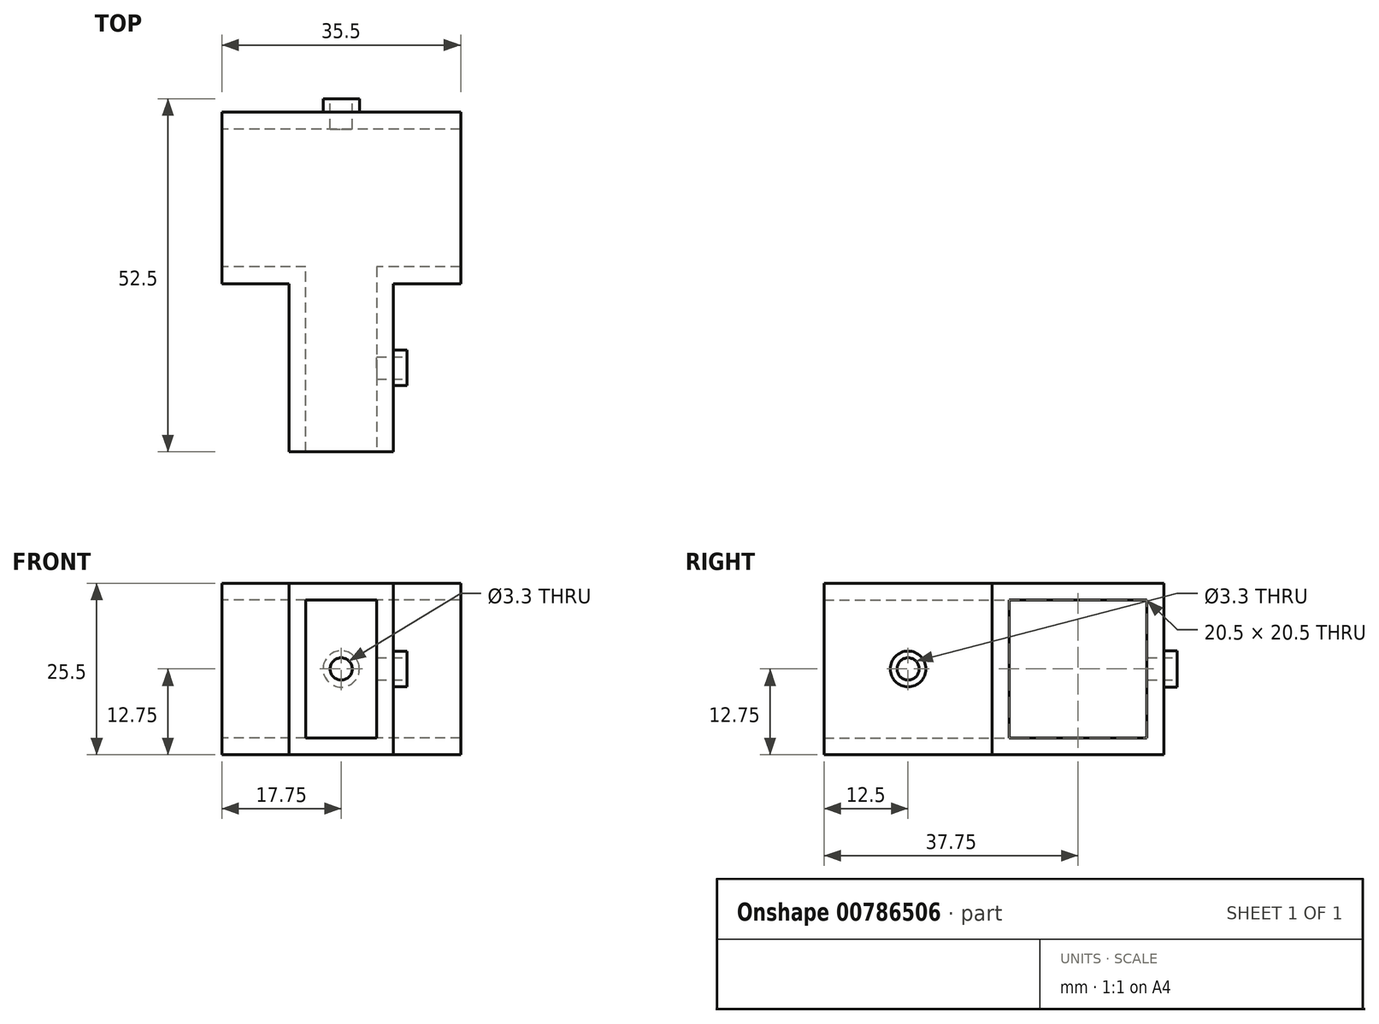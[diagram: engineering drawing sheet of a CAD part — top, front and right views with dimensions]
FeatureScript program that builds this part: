
annotation { "Feature Type Name" : "Feature", "Feature Type Description" : "" }
export const myFeature = defineFeature(function(context is Context, id is Id, definition is map)
    precondition{}
    {
        {
            var Q0;
            Q0=qCreatedBy(makeId("Front.planeOp"),FACE);
            var sketch = newSketch(context, id + "F0", { "sketchPlane" : qUnion([Q0])});
            skLineSegment(sketch, "E0.bottom", {"start": v(-17.75, 12.75) * mm, "end": v(17.75, 12.75) * mm});
            skLineSegment(sketch, "E0.top", {"start": v(-17.75, -12.75) * mm, "end": v(17.75, -12.75) * mm});
            skLineSegment(sketch, "E0.left", {"start": v(-17.75, 15.55) * mm, "end": v(-17.75, -12.75) * mm});
            skLineSegment(sketch, "E0.right", {"start": v(17.75, 12.75) * mm, "end": v(17.75, -12.75) * mm});
            skPoint(sketch, "E1", {"position": v(0, 0) * mm});
            skPoint(sketch, "E1.positionSnap0", {"position": v(17.75, 0) * mm});
            skPoint(sketch, "E1.positionSnap1", {"position": v(0, 12.75) * mm});
            skSolve(sketch);
        }
        {
            var Q0;
            Q0=qSketchRegion(id+"F0",true);
            extrude(context, id + "F1", {"entities" : qUnion([Q0]), "depth" : 25.5 * mm, "offsetDistance" : 25 * mm});
        }
        {
            var Q0;
            Q0=makeQuery(id+"F1.opExtrude","SWEPT_FACE",FACE,{"disambiguationData":[OSD([sQuery(id+"F0.wireOp",EDGE,"E0.left")])]});
            var sketch = newSketch(context, id + "F2", { "sketchPlane" : qUnion([Q0])});
            skLineSegment(sketch, "E2.bottom", {"start": v(2.5, 10.25) * mm, "end": v(23, 10.25) * mm});
            skLineSegment(sketch, "E2.top", {"start": v(2.5, -10.25) * mm, "end": v(23, -10.25) * mm});
            skLineSegment(sketch, "E2.left", {"start": v(2.5, 10.25) * mm, "end": v(2.5, -10.25) * mm});
            skLineSegment(sketch, "E2.right", {"start": v(23, 10.25) * mm, "end": v(23, -10.25) * mm});
            skSolve(sketch);
        }
        {
            var Q0;
            Q0=qSketchRegion(id+"F2",true);
            extrude(context, id + "F3", {"entities" : qUnion([Q0]), "operationType" : NewBodyOperationType.REMOVE, "oppositeDirection" : true, "depth" : 35.5 * mm, "offsetDistance" : 25 * mm});
        }
        {
            var Q0;
            Q0=makeQuery(id+"F1.opExtrude","CAP_FACE",FACE,{"disambiguationData":[OSD([sQuery(id+"F0.wireOp",EDGE,"E0.bottom"),sQuery(id+"F0.wireOp",EDGE,"E0.top"),sQuery(id+"F0.wireOp",EDGE,"E0.left"),sQuery(id+"F0.wireOp",EDGE,"E0.right")])],"isStart":false});
            var sketch = newSketch(context, id + "F4", { "sketchPlane" : qUnion([Q0])});
            skLineSegment(sketch, "E3.bottom", {"start": v(-7.75, 12.75) * mm, "end": v(7.75, 12.75) * mm});
            skLineSegment(sketch, "E3.top", {"start": v(-7.75, -12.75) * mm, "end": v(7.75, -12.75) * mm});
            skLineSegment(sketch, "E3.left", {"start": v(-7.75, 12.75) * mm, "end": v(-7.75, -12.75) * mm});
            skLineSegment(sketch, "E3.right", {"start": v(7.75, 12.75) * mm, "end": v(7.75, -12.75) * mm});
            skSolve(sketch);
        }
        {
            var Q0;
            Q0=qSketchRegion(id+"F4",true);
            extrude(context, id + "F5", {"entities" : qUnion([Q0]), "operationType" : NewBodyOperationType.ADD, "depth" : 25 * mm, "offsetDistance" : 25 * mm});
        }
        {
            var Q0;
            Q0=makeQuery(id+"F5.opExtrude","CAP_FACE",FACE,{"disambiguationData":[OSD([sQuery(id+"F4.wireOp",EDGE,"E3.bottom"),sQuery(id+"F4.wireOp",EDGE,"E3.top"),sQuery(id+"F4.wireOp",EDGE,"E3.left"),sQuery(id+"F4.wireOp",EDGE,"E3.right")])],"isStart":false});
            var sketch = newSketch(context, id + "F6", { "sketchPlane" : qUnion([Q0])});
            skLineSegment(sketch, "E4.bottom", {"start": v(-15.25, 10.25) * mm, "end": v(5.25, 10.25) * mm});
            skLineSegment(sketch, "E4.top", {"start": v(-15.25, -10.25) * mm, "end": v(5.25, -10.25) * mm});
            skLineSegment(sketch, "E4.left", {"start": v(-15.25, 10.25) * mm, "end": v(-15.25, -10.25) * mm});
            skLineSegment(sketch, "E4.right", {"start": v(5.25, 10.25) * mm, "end": v(5.25, -10.25) * mm});
            skSolve(sketch);
        }
        {
            var Q0;
            Q0=qSketchRegion(id+"F6",true);
            extrude(context, id + "F7", {"entities" : qUnion([Q0]), "operationType" : NewBodyOperationType.REMOVE, "oppositeDirection" : true, "depth" : 38 * mm, "offsetDistance" : 25 * mm});
        }
        {
            var Q0;
            Q0=makeQuery(id+"F5.opExtrude","SWEPT_FACE",FACE,{"disambiguationData":[OSD([sQuery(id+"F4.wireOp",EDGE,"E3.right")])]});
            var sketch = newSketch(context, id + "F8", { "sketchPlane" : qUnion([Q0])});
            skCircle(sketch, "E5", {"center": v(-38, 0) * mm, "radius": 2.65 * mm});
            skPoint(sketch, "E5.centerSnap0", {"position": v(-38, -12.75) * mm});
            skPoint(sketch, "E5.centerSnap1", {"position": v(-50.5, 0) * mm});
            skSolve(sketch);
        }
        {
            var Q0;
            Q0=qSketchRegion(id+"F8",true);
            extrude(context, id + "F9", {"entities" : qUnion([Q0]), "operationType" : NewBodyOperationType.ADD, "depth" : 2 * mm, "offsetDistance" : 25 * mm});
        }
        {
            var Q0;
            Q0=makeQuery(id+"F9.opExtrude","CAP_FACE",FACE,{"disambiguationData":[OSD([sQuery(id+"F8.wireOp",EDGE,"E5")])],"isStart":false});
            var sketch = newSketch(context, id + "F10", { "sketchPlane" : qUnion([Q0])});
            skCircle(sketch, "E6", {"center": v(-38, 0) * mm, "radius": 1.65 * mm});
            skSolve(sketch);
        }
        {
            var Q0;
            Q0=qSketchRegion(id+"F10",true);
            extrude(context, id + "F11", {"entities" : qUnion([Q0]), "operationType" : NewBodyOperationType.REMOVE, "endBound" : BoundingType.THROUGH_ALL, "oppositeDirection" : true, "depth" : 30 * mm, "offsetDistance" : 25 * mm});
        }
        {
            var Q0;
            Q0=makeQuery(id+"F1.opExtrude","CAP_FACE",FACE,{"disambiguationData":[OSD([sQuery(id+"F0.wireOp",EDGE,"E0.bottom"),sQuery(id+"F0.wireOp",EDGE,"E0.top"),sQuery(id+"F0.wireOp",EDGE,"E0.left"),sQuery(id+"F0.wireOp",EDGE,"E0.right")])],"isStart":true});
            var sketch = newSketch(context, id + "F12", { "sketchPlane" : qUnion([Q0])});
            skCircle(sketch, "E7", {"center": v(0, 0) * mm, "radius": 2.7 * mm});
            skSolve(sketch);
        }
        {
            var Q0;
            Q0=qSketchRegion(id+"F12",true);
            extrude(context, id + "F13", {"entities" : qUnion([Q0]), "operationType" : NewBodyOperationType.ADD, "depth" : 2 * mm, "offsetDistance" : 25 * mm});
        }
        {
            var Q0;
            Q0=makeQuery(id+"F13.opExtrude","CAP_FACE",FACE,{"disambiguationData":[OSD([sQuery(id+"F12.wireOp",EDGE,"E7")])],"isStart":false});
            var sketch = newSketch(context, id + "F14", { "sketchPlane" : qUnion([Q0])});
            skCircle(sketch, "E8", {"center": v(0, 0) * mm, "radius": 1.65 * mm});
            skSolve(sketch);
        }
        {
            var Q0;
            Q0=qSketchRegion(id+"F14",true);
            extrude(context, id + "F15", {"entities" : qUnion([Q0]), "operationType" : NewBodyOperationType.REMOVE, "oppositeDirection" : true, "depth" : 5.5 * mm, "offsetDistance" : 25 * mm});
        }
        {
            var Q0;
            Q0=makeQuery(id+"F7.boolean.opBoolean","MERGE",FACE,{"derivedFrom":[makeQuery(id+"F3.boolean.opBoolean","COPY",FACE,{"derivedFrom":makeQuery(id+"F3.opExtrude","SWEPT_FACE",FACE,{"disambiguationData":[OSD([sQuery(id+"F2.wireOp",EDGE,"E2.top")])]})}),makeQuery(id+"F7.opExtrude","SWEPT_FACE",FACE,{"disambiguationData":[OSD([sQuery(id+"F6.wireOp",EDGE,"E4.top")])]})]});
            var sketch = newSketch(context, id + "F16", { "sketchPlane" : qUnion([Q0])});
            skLineSegment(sketch, "E9.bottom", {"start": v(-7.75, -50.5) * mm, "end": v(-5.25, -50.5) * mm});
            skLineSegment(sketch, "E9.top", {"start": v(-7.75, -25.5) * mm, "end": v(-5.25, -25.5) * mm});
            skLineSegment(sketch, "E9.left", {"start": v(-7.75, -50.5) * mm, "end": v(-7.75, -25.5) * mm});
            skLineSegment(sketch, "E9.right", {"start": v(-5.25, -50.5) * mm, "end": v(-5.25, -25.5) * mm});
            skSolve(sketch);
        }
        {
            var Q0;
            Q0 = qSketchRegion(id + "F16", true);
            extrude(context, id + "F17", {"entities" : qUnion([Q0]), "operationType" : NewBodyOperationType.ADD, "depth" : 20.5 * mm, "offsetDistance" : 25 * mm});
        }
        {
            var Q0;
            {var subQ0=sQuery(id+"F4.wireOp",EDGE,"E3.left");var subQ4=sQuery(id+"F0.wireOp",EDGE,"E0.top");var subQ5=sQuery(id+"F0.wireOp",EDGE,"E0.bottom");var subQ7=makeQuery(id+"F5.opExtrude","SWEPT_FACE",FACE,{"disambiguationData":[OSD([subQ0])]});Q0=makeQuery(id+"F17.boolean.opBoolean","MERGE",FACE,{"derivedFrom":[makeQuery(id+"F7.boolean.opBoolean","SPLIT",FACE,{"disambiguationData":[TD([makeQuery(id+"F1.opExtrude","SWEPT_FACE",FACE,{"disambiguationData":[OSD([subQ5])]})])],"derivedFrom":subQ7}),makeQuery(id+"F7.boolean.opBoolean","SPLIT",FACE,{"disambiguationData":[TD([makeQuery(id+"F1.opExtrude","SWEPT_FACE",FACE,{"disambiguationData":[OSD([subQ4])]})])],"derivedFrom":subQ7}),makeQuery(id+"F17.opExtrude","SWEPT_FACE",FACE,{"disambiguationData":[OSD([sQuery(id+"F16.wireOp",EDGE,"E9.left")])]})]});}
            var sketch = newSketch(context, id + "F18", { "sketchPlane" : qUnion([Q0])});
            skLineSegment(sketch, "E10.bottom", {"start": v(28, 10.25) * mm, "end": v(48, 10.25) * mm});
            skLineSegment(sketch, "E10.top", {"start": v(28, -10.25) * mm, "end": v(48, -10.25) * mm});
            skLineSegment(sketch, "E10.left", {"start": v(28, 10.25) * mm, "end": v(28, -10.25) * mm});
            skLineSegment(sketch, "E10.right", {"start": v(48, 10.25) * mm, "end": v(48, -10.25) * mm});
            skSolve(sketch);
        }
        {
            var Q0;
            Q0 = qSketchRegion(id + "F18", true);
            extrude(context, id + "F19", {"entities" : qUnion([Q0]), "operationType" : NewBodyOperationType.REMOVE, "oppositeDirection" : true, "depth" : 2.5 * mm, "offsetDistance" : 25 * mm});
        }
        {
            var Q0;
            Q0=makeQuery(id+"F19.boolean.opBoolean","MERGE",FACE,{"derivedFrom":[makeQuery(id+"F7.boolean.opBoolean","MERGE",FACE,{"derivedFrom":[makeQuery(id+"F3.boolean.opBoolean","COPY",FACE,{"derivedFrom":makeQuery(id+"F3.opExtrude","SWEPT_FACE",FACE,{"disambiguationData":[OSD([sQuery(id+"F2.wireOp",EDGE,"E2.top")])]})}),makeQuery(id+"F7.opExtrude","SWEPT_FACE",FACE,{"disambiguationData":[OSD([sQuery(id+"F6.wireOp",EDGE,"E4.top")])]})]}),makeQuery(id+"F19.opExtrude","SWEPT_FACE",FACE,{"disambiguationData":[OSD([sQuery(id+"F18.wireOp",EDGE,"E10.top")])]})]});
            var sketch = newSketch(context, id + "F20", { "sketchPlane" : qUnion([Q0])});
            skLineSegment(sketch, "E11.bottom", {"start": v(-7.75, -37) * mm, "end": v(-5.25, -37) * mm});
            skLineSegment(sketch, "E11.top", {"start": v(-7.75, -39.5) * mm, "end": v(-5.25, -39.5) * mm});
            skLineSegment(sketch, "E11.left", {"start": v(-7.75, -37) * mm, "end": v(-7.75, -39.5) * mm});
            skLineSegment(sketch, "E11.right", {"start": v(-5.25, -37) * mm, "end": v(-5.25, -39.5) * mm});
            skSolve(sketch);
        }
        {
            var Q0;
            Q0 = qSketchRegion(id + "F20", true);
            extrude(context, id + "F21", {"entities" : qUnion([Q0]), "operationType" : NewBodyOperationType.ADD, "depth" : 20.5 * mm, "offsetDistance" : 25 * mm});
        }
        {
            var Q0;
            {var subQ0=sQuery(id+"F0.wireOp",EDGE,"E0.top");var subQ1=sQuery(id+"F0.wireOp",EDGE,"E0.right");var subQ2=sQuery(id+"F0.wireOp",EDGE,"E0.bottom");Q0=makeQuery(id+"F5.boolean.opBoolean","SPLIT",FACE,{"disambiguationData":[TD([makeQuery(id+"F1.opExtrude","SWEPT_FACE",FACE,{"disambiguationData":[OSD([subQ1])]})])],"derivedFrom":makeQuery(id+"F1.opExtrude","CAP_FACE",FACE,{"disambiguationData":[OSD([subQ2,subQ0,sQuery(id+"F0.wireOp",EDGE,"E0.left"),subQ1])],"isStart":false})});}
            var sketch = newSketch(context, id + "F22", { "sketchPlane" : qUnion([Q0])});
            skLineSegment(sketch, "E12.bottom", {"start": v(7.75, 10.25) * mm, "end": v(15.25, 10.25) * mm});
            skLineSegment(sketch, "E12.top", {"start": v(7.75, -10.25) * mm, "end": v(15.25, -10.25) * mm});
            skLineSegment(sketch, "E12.left", {"start": v(7.75, 10.25) * mm, "end": v(7.75, -10.25) * mm});
            skLineSegment(sketch, "E12.right", {"start": v(15.25, 10.25) * mm, "end": v(15.25, -10.25) * mm});
            skSolve(sketch);
        }
        {
            var Q0;
            Q0 = qSketchRegion(id + "F22", true);
            extrude(context, id + "F23", {"entities" : qUnion([Q0]), "operationType" : NewBodyOperationType.REMOVE, "oppositeDirection" : true, "depth" : 2.5 * mm, "offsetDistance" : 25 * mm});
        }
        {
            var Q0;
            {var subQ0=sQuery(id+"F0.wireOp",EDGE,"E0.left");var subQ1=sQuery(id+"F0.wireOp",EDGE,"E0.top");var subQ2=sQuery(id+"F0.wireOp",EDGE,"E0.bottom");Q0=makeQuery(id+"F5.boolean.opBoolean","SPLIT",FACE,{"disambiguationData":[TD([makeQuery(id+"F1.opExtrude","SWEPT_FACE",FACE,{"disambiguationData":[OSD([subQ0])]})])],"derivedFrom":makeQuery(id+"F1.opExtrude","CAP_FACE",FACE,{"disambiguationData":[OSD([subQ2,subQ1,subQ0,sQuery(id+"F0.wireOp",EDGE,"E0.right")])],"isStart":false})});}
            var sketch = newSketch(context, id + "F24", { "sketchPlane" : qUnion([Q0])});
            skLineSegment(sketch, "E13.bottom", {"start": v(-15.25, 10.25) * mm, "end": v(-5.25, 10.25) * mm});
            skLineSegment(sketch, "E13.top", {"start": v(-15.25, -10.25) * mm, "end": v(-5.25, -10.25) * mm});
            skLineSegment(sketch, "E13.left", {"start": v(-15.25, 10.25) * mm, "end": v(-15.25, -10.25) * mm});
            skLineSegment(sketch, "E13.right", {"start": v(-5.25, 10.25) * mm, "end": v(-5.25, -10.25) * mm});
            skSolve(sketch);
        }
        {
            var Q0;
            Q0 = qSketchRegion(id + "F24", true);
            extrude(context, id + "F25", {"entities" : qUnion([Q0]), "operationType" : NewBodyOperationType.ADD, "oppositeDirection" : true, "depth" : 2.5 * mm, "offsetDistance" : 25 * mm});
        }
        {
            var Q0;
            {var subQ0=sQuery(id+"F0.wireOp",EDGE,"E0.top");var subQ1=sQuery(id+"F0.wireOp",EDGE,"E0.right");var subQ2=sQuery(id+"F0.wireOp",EDGE,"E0.bottom");Q0=makeQuery(id+"F5.boolean.opBoolean","SPLIT",FACE,{"disambiguationData":[TD([makeQuery(id+"F1.opExtrude","SWEPT_FACE",FACE,{"disambiguationData":[OSD([subQ1])]})])],"derivedFrom":makeQuery(id+"F1.opExtrude","CAP_FACE",FACE,{"disambiguationData":[OSD([subQ2,subQ0,sQuery(id+"F0.wireOp",EDGE,"E0.left"),subQ1])],"isStart":false})});}
            var sketch = newSketch(context, id + "F26", { "sketchPlane" : qUnion([Q0])});
            skLineSegment(sketch, "E14.bottom", {"start": v(15.25, 10.25) * mm, "end": v(5.25, 10.25) * mm});
            skLineSegment(sketch, "E14.top", {"start": v(15.25, -10.25) * mm, "end": v(5.25, -10.25) * mm});
            skLineSegment(sketch, "E14.left", {"start": v(15.25, 10.25) * mm, "end": v(15.25, -10.25) * mm});
            skLineSegment(sketch, "E14.right", {"start": v(5.25, 10.25) * mm, "end": v(5.25, -10.25) * mm});
            skSolve(sketch);
        }
        {
            var Q0;
            Q0 = qSketchRegion(id + "F26", true);
            extrude(context, id + "F27", {"entities" : qUnion([Q0]), "operationType" : NewBodyOperationType.ADD, "oppositeDirection" : true, "depth" : 2.5 * mm, "offsetDistance" : 25 * mm});
        }
        {
            var Q0;
            {var subQ0=sQuery(id+"F4.wireOp",EDGE,"E3.left");var subQ4=sQuery(id+"F0.wireOp",EDGE,"E0.top");var subQ5=sQuery(id+"F0.wireOp",EDGE,"E0.bottom");var subQ7=makeQuery(id+"F5.opExtrude","SWEPT_FACE",FACE,{"disambiguationData":[OSD([subQ0])]});Q0=makeQuery(id+"F21.boolean.opBoolean","MERGE",FACE,{"derivedFrom":[makeQuery(id+"F17.boolean.opBoolean","MERGE",FACE,{"derivedFrom":[makeQuery(id+"F7.boolean.opBoolean","SPLIT",FACE,{"disambiguationData":[TD([makeQuery(id+"F1.opExtrude","SWEPT_FACE",FACE,{"disambiguationData":[OSD([subQ5])]})])],"derivedFrom":subQ7}),makeQuery(id+"F7.boolean.opBoolean","SPLIT",FACE,{"disambiguationData":[TD([makeQuery(id+"F1.opExtrude","SWEPT_FACE",FACE,{"disambiguationData":[OSD([subQ4])]})])],"derivedFrom":subQ7}),makeQuery(id+"F17.opExtrude","SWEPT_FACE",FACE,{"disambiguationData":[OSD([sQuery(id+"F16.wireOp",EDGE,"E9.left")])]})]}),makeQuery(id+"F21.opExtrude","SWEPT_FACE",FACE,{"disambiguationData":[OSD([sQuery(id+"F20.wireOp",EDGE,"E11.left")])]})]});}
            var sketch = newSketch(context, id + "F28", { "sketchPlane" : qUnion([Q0])});
            skLineSegment(sketch, "E15.bottom", {"start": v(28, 10.25) * mm, "end": v(37, 10.25) * mm});
            skLineSegment(sketch, "E15.top", {"start": v(28, -10.25) * mm, "end": v(37, -10.25) * mm});
            skLineSegment(sketch, "E15.left", {"start": v(28, 10.25) * mm, "end": v(28, -10.25) * mm});
            skLineSegment(sketch, "E15.right", {"start": v(37, 10.25) * mm, "end": v(37, -10.25) * mm});
            skLineSegment(sketch, "E16.bottom", {"start": v(39.5, 10.25) * mm, "end": v(48, 10.25) * mm});
            skLineSegment(sketch, "E16.top", {"start": v(39.5, -10.25) * mm, "end": v(48, -10.25) * mm});
            skLineSegment(sketch, "E16.left", {"start": v(39.5, 10.25) * mm, "end": v(39.5, -10.25) * mm});
            skLineSegment(sketch, "E16.right", {"start": v(48, 10.25) * mm, "end": v(48, -10.25) * mm});
            skSolve(sketch);
        }
        {
            var Q0;
            Q0 = qSketchRegion(id + "F28", true);
            extrude(context, id + "F29", {"entities" : qUnion([Q0]), "operationType" : NewBodyOperationType.ADD, "oppositeDirection" : true, "depth" : 2.5 * mm, "offsetDistance" : 25 * mm});
        }
    });
